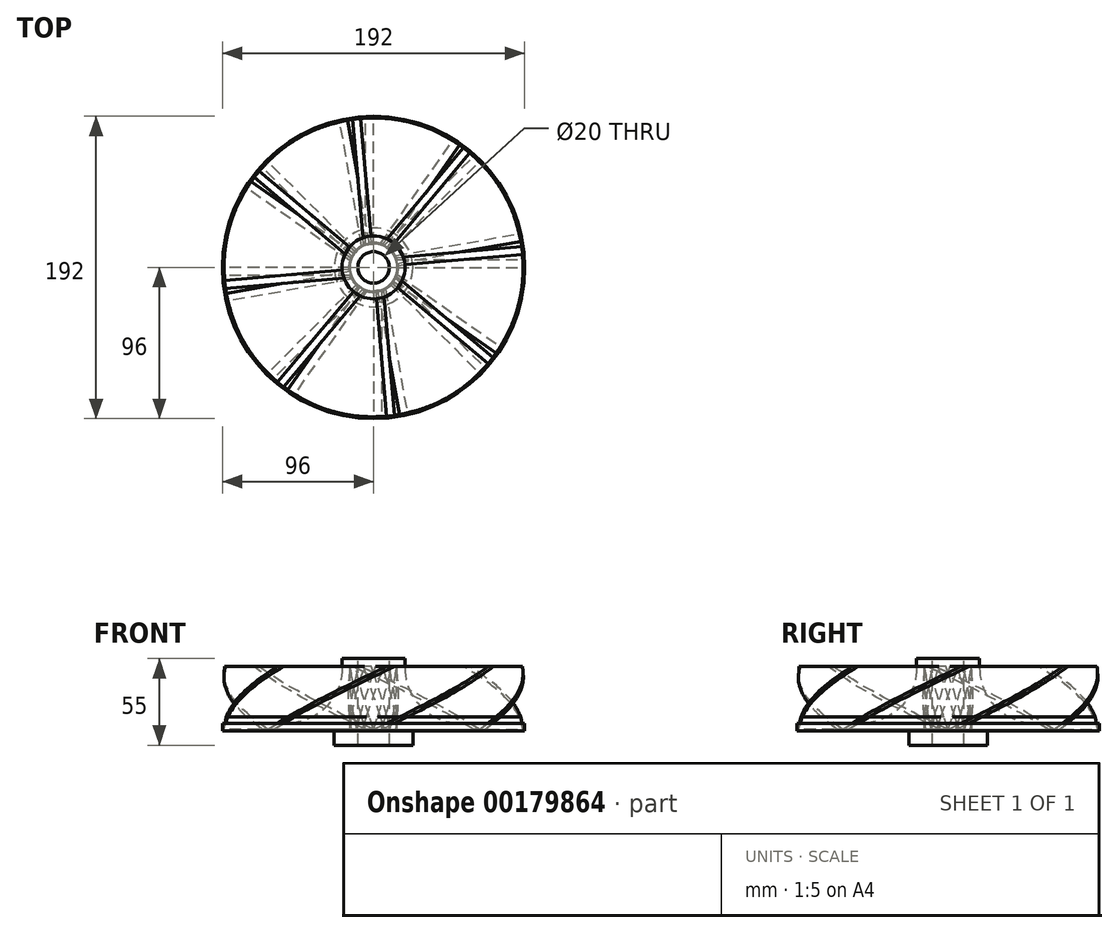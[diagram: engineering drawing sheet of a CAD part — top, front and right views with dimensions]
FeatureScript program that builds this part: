
annotation { "Feature Type Name" : "Feature", "Feature Type Description" : "" }
export const myFeature = defineFeature(function(context is Context, id is Id, definition is map)
    precondition{}
    {
        {
            var Q0;
            Q0=qCreatedBy(makeId("Top.planeOp"),FACE);
            var sketch = newSketch(context, id + "F0", { "sketchPlane" : qUnion([Q0])});
            skLineSegment(sketch, "E0.bottom", {"start": v(15, 0) * mm, "end": v(95, 0) * mm});
            skLineSegment(sketch, "E0.top", {"start": v(15, 5) * mm, "end": v(95, 5) * mm});
            skLineSegment(sketch, "E0.left", {"start": v(15, 0) * mm, "end": v(15, 5) * mm});
            skLineSegment(sketch, "E0.right", {"start": v(95, 0) * mm, "end": v(95, 5) * mm});
            skSolve(sketch);
        }
        {
            var Q0;
            Q0=qCreatedBy(makeId("Top.planeOp"),FACE);
            cPlane(context, id + "F1", {"entities" : qUnion([Q0]), "cplaneType" : CPlaneType.OFFSET, "offset" : 8 * mm, "width" : 150 * mm, "height" : 150 * mm});
        }
        {
            var Q0;
            Q0=qCreatedBy(id+"F1.planeOp",FACE);
            var sketch = newSketch(context, id + "F2", { "sketchPlane" : qUnion([Q0])});
            skLineSegment(sketch, "E1", {"start": v(14.77, 2.6) * mm, "end": v(93.56, 16.5) * mm});
            skLineSegment(sketch, "E2.0", {"start": v(13.9, 7.53) * mm, "end": v(92.69, 21.42) * mm});
            skLineSegment(sketch, "E3.0", {"start": v(14.77, 2.6) * mm, "end": v(13.9, 7.53) * mm});
            skLineSegment(sketch, "E4.0", {"start": v(93.56, 16.5) * mm, "end": v(92.69, 21.42) * mm});
            skPoint(sketch, "E5.start.orphan", {"position": v(113.1, 0) * mm});
            skSolve(sketch);
        }
        {
            var Q0;
            Q0=qCreatedBy(makeId("Top.planeOp"),FACE);
            cPlane(context, id + "F3", {"entities" : qUnion([Q0]), "cplaneType" : CPlaneType.OFFSET, "offset" : 16 * mm, "width" : 150 * mm, "height" : 150 * mm});
        }
        {
            var Q0;
            Q0=qCreatedBy(id+"F3.planeOp",FACE);
            var sketch = newSketch(context, id + "F4", { "sketchPlane" : qUnion([Q0])});
            skLineSegment(sketch, "E6", {"start": v(14.1, 5.13) * mm, "end": v(89.27, 32.5) * mm});
            skLineSegment(sketch, "E7.0", {"start": v(12.39, 9.83) * mm, "end": v(87.56, 37.2) * mm});
            skLineSegment(sketch, "E8.0", {"start": v(12.39, 9.83) * mm, "end": v(14.1, 5.13) * mm});
            skLineSegment(sketch, "E9.0", {"start": v(87.56, 37.2) * mm, "end": v(89.27, 32.5) * mm});
            skPoint(sketch, "E10.start.orphan", {"position": v(108.67, 0) * mm});
            skSolve(sketch);
        }
        {
            var Q0;
            Q0=qCreatedBy(makeId("Top.planeOp"),FACE);
            cPlane(context, id + "F5", {"entities" : qUnion([Q0]), "cplaneType" : CPlaneType.OFFSET, "offset" : 24 * mm, "width" : 150 * mm, "height" : 150 * mm});
        }
        {
            var Q0;
            Q0=qCreatedBy(id+"F5.planeOp",FACE);
            var sketch = newSketch(context, id + "F6", { "sketchPlane" : qUnion([Q0])});
            skLineSegment(sketch, "E11", {"start": v(13, 7.5) * mm, "end": v(82.27, 47.5) * mm});
            skLineSegment(sketch, "E12.0", {"start": v(10.5, 11.83) * mm, "end": v(79.77, 51.83) * mm});
            skLineSegment(sketch, "E13.0", {"start": v(10.5, 11.83) * mm, "end": v(13, 7.5) * mm});
            skLineSegment(sketch, "E14.0", {"start": v(79.77, 51.83) * mm, "end": v(82.27, 47.5) * mm});
            skPoint(sketch, "E15.start.orphan", {"position": v(108.59, 0) * mm});
            skSolve(sketch);
        }
        {
            var Q0;
            Q0=qCreatedBy(makeId("Top.planeOp"),FACE);
            cPlane(context, id + "F7", {"entities" : qUnion([Q0]), "cplaneType" : CPlaneType.OFFSET, "offset" : 32 * mm, "width" : 150 * mm, "height" : 150 * mm});
        }
        {
            var Q0;
            Q0=qCreatedBy(id+"F7.planeOp",FACE);
            var sketch = newSketch(context, id + "F8", { "sketchPlane" : qUnion([Q0])});
            skLineSegment(sketch, "E16", {"start": v(11.5, 9.64) * mm, "end": v(72.77, 61.06) * mm});
            skLineSegment(sketch, "E17.0", {"start": v(8.28, 13.47) * mm, "end": v(69.56, 64.9) * mm});
            skLineSegment(sketch, "E18.0", {"start": v(8.28, 13.47) * mm, "end": v(11.5, 9.64) * mm});
            skLineSegment(sketch, "E19.0", {"start": v(69.56, 64.9) * mm, "end": v(72.77, 61.06) * mm});
            skPoint(sketch, "E20.start.orphan", {"position": v(107.22, 0) * mm});
            skSolve(sketch);
        }
        {
            var Q0;
            Q0=qCreatedBy(makeId("Top.planeOp"),FACE);
            cPlane(context, id + "F9", {"entities" : qUnion([Q0]), "cplaneType" : CPlaneType.OFFSET, "offset" : 40 * mm, "width" : 150 * mm, "height" : 150 * mm});
        }
        {
            var Q0;
            Q0=qCreatedBy(id+"F9.planeOp",FACE);
            var sketch = newSketch(context, id + "F10", { "sketchPlane" : qUnion([Q0])});
            skLineSegment(sketch, "E21", {"start": v(9.64, 11.5) * mm, "end": v(61.06, 72.77) * mm});
            skLineSegment(sketch, "E22.0", {"start": v(5.81, 14.7) * mm, "end": v(57.23, 75.99) * mm});
            skLineSegment(sketch, "E23.0", {"start": v(9.64, 11.5) * mm, "end": v(5.81, 14.7) * mm});
            skLineSegment(sketch, "E24.0", {"start": v(61.06, 72.77) * mm, "end": v(57.23, 75.99) * mm});
            skPoint(sketch, "E25.start.orphan", {"position": v(94.59, 0) * mm});
            skSolve(sketch);
        }
        {
            var Q0;
            Q0=makeQuery(id+"F0.imprint","IMPRINT",FACE,{"disambiguationData":[TD([[makeQuery(id+"F0.imprint","IMPRINT",EDGE,{"derivedFrom":sQuery(id+"F0.wireOp",EDGE,"E0.bottom")}),1.0]])]});
            var Q1;
            Q1=makeQuery(id+"F2.imprint","IMPRINT",FACE,{"disambiguationData":[TD([[makeQuery(id+"F2.imprint","IMPRINT",EDGE,{"derivedFrom":sQuery(id+"F2.wireOp",EDGE,"E1")}),1.0]])]});
            loft(context, id + "F11", {"sheetProfilesArray" : [{ "sheetProfileEntities" : qUnion([Q0]) }, { "sheetProfileEntities" : qUnion([Q1]) }]});
        }
        {
            var Q1;
            Q1=makeQuery(id+"F11.opLoft","CAP_FACE",FACE,{"disambiguationData":[OSD([makeQuery(id+"F2.imprint","IMPRINT",FACE,{"disambiguationData":[TD([[makeQuery(id+"F2.imprint","IMPRINT",EDGE,{"derivedFrom":sQuery(id+"F2.wireOp",EDGE,"E1")}),1.0]])]})])],"isStart":true});
            var Q2;
            Q2=makeQuery(id+"F4.imprint","IMPRINT",FACE,{"disambiguationData":[TD([[makeQuery(id+"F4.imprint","IMPRINT",EDGE,{"derivedFrom":sQuery(id+"F4.wireOp",EDGE,"E6")}),1.0]])]});
            var Q3;
            Q3=makeQuery(id+"F6.imprint","IMPRINT",FACE,{"disambiguationData":[TD([[makeQuery(id+"F6.imprint","IMPRINT",EDGE,{"derivedFrom":sQuery(id+"F6.wireOp",EDGE,"E11")}),1.0]])]});
            var Q4;
            Q4=makeQuery(id+"F8.imprint","IMPRINT",FACE,{"disambiguationData":[TD([[makeQuery(id+"F8.imprint","IMPRINT",EDGE,{"derivedFrom":sQuery(id+"F8.wireOp",EDGE,"E16")}),1.0]])]});
            var Q5;
            Q5=makeQuery(id+"F10.imprint","IMPRINT",FACE,{"disambiguationData":[TD([[makeQuery(id+"F10.imprint","IMPRINT",EDGE,{"derivedFrom":sQuery(id+"F10.wireOp",EDGE,"E21")}),1.0]])]});
            loft(context, id + "F12", {"operationType" : NewBodyOperationType.ADD, "sheetProfilesArray" : [{ "sheetProfileEntities" : qUnion([Q1]) }, { "sheetProfileEntities" : qUnion([Q2]) }, { "sheetProfileEntities" : qUnion([Q3]) }, { "sheetProfileEntities" : qUnion([Q4]) }, { "sheetProfileEntities" : qUnion([Q5]) }]});
        }
        {
            var Q0;
            Q0=qCreatedBy(makeId("Right.planeOp"),FACE);
            var sketch = newSketch(context, id + "F13", { "sketchPlane" : qUnion([Q0])});
            skLineSegment(sketch, "E26", {"start": v(0, 0) * mm, "end": v(0, 89.79) * mm, "construction": true});
            skSolve(sketch);
        }
        {
            var Q0;
            Q0=makeQuery(id+"F11.opLoft","SWEPT_BODY",BODY,{"disambiguationData":[OSD([makeQuery(id+"F0.imprint","IMPRINT",FACE,{"disambiguationData":[TD([[makeQuery(id+"F0.imprint","IMPRINT",EDGE,{"derivedFrom":sQuery(id+"F0.wireOp",EDGE,"E0.bottom")}),1.0]])]}),makeQuery(id+"F2.imprint","IMPRINT",FACE,{"disambiguationData":[TD([[makeQuery(id+"F2.imprint","IMPRINT",EDGE,{"derivedFrom":sQuery(id+"F2.wireOp",EDGE,"E1")}),1.0]])]})])]});
            var Q1;
            Q1=sQuery(id+"F13.wireOp",EDGE,"E26");
            circularPattern(context, id + "F14", {"entities" : qUnion([Q0]), "axis" : qUnion([Q1]), "angle" : 45 * degree, "instanceCount" : 8});
        }
        {
            var Q0;
            Q0=qCreatedBy(makeId("Front.planeOp"),FACE);
            var sketch = newSketch(context, id + "F15", { "sketchPlane" : qUnion([Q0])});
            skLineSegment(sketch, "E27", {"start": v(-10, -10) * mm, "end": v(-10, 45) * mm});
            skLineSegment(sketch, "E28", {"start": v(-10, 45) * mm, "end": v(-20, 45) * mm});
            skLineSegment(sketch, "E29", {"start": v(-20, 45) * mm, "end": v(-20, 39) * mm});
            skLineSegment(sketch, "E30", {"start": v(-55, 4) * mm, "end": v(-96, 4) * mm});
            skLineSegment(sketch, "E31", {"start": v(-96, 4) * mm, "end": v(-96, -1) * mm});
            skLineSegment(sketch, "E32", {"start": v(-96, -1) * mm, "end": v(-25, -1) * mm});
            skLineSegment(sketch, "E33", {"start": v(-25, -1) * mm, "end": v(-25, -10) * mm});
            skLineSegment(sketch, "E34", {"start": v(-25, -10) * mm, "end": v(-10, -10) * mm});
            skPoint(sketch, "E35.visualSharp", {"position": v(-20, 4) * mm});
            skArc(sketch, "E35.filletArc", {"start": v(-55, 4) * mm, "mid": v(-30.25, 14.25) * mm, "end": v(-20, 39) * mm});
            skSolve(sketch);
        }
        {
            var Q0;
            Q0=qCreatedBy(makeId("Front.planeOp"),FACE);
            var sketch = newSketch(context, id + "F16", { "sketchPlane" : qUnion([Q0])});
            skLineSegment(sketch, "E36", {"start": v(0, 66.86) * mm, "end": v(0, -49.46) * mm, "construction": true});
            skSolve(sketch);
        }
        {
            var Q0;
            Q0 = qSketchRegion(id + "F16", true);
            var Q1;
            Q1=makeQuery(id+"F15.imprint","IMPRINT",FACE,{"disambiguationData":[TD([[makeQuery(id+"F15.imprint","IMPRINT",EDGE,{"derivedFrom":sQuery(id+"F15.wireOp",EDGE,"E27")}),1.0]])]});
            var Q2;
            Q2=sQuery(id+"F16.wireOp",EDGE,"E36");
            revolve(context, id + "F17", {"entities" : qUnion([Q0, Q1]), "axis" : qUnion([Q2]), "revolveType" : RevolveType.FULL});
        }
    });
